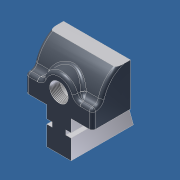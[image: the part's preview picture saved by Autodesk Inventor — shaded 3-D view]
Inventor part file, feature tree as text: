
AUTODESK INVENTOR PART (.ipt)
format: ipt  version: unknown  size: 439,296 bytes
history: native  units: in
note: dims shown in document units (in); Inventor stores cm internally (conversion verified against a paired STEP export)
features: sketch x11, hole x6, extrude x5, fillet x5, projected_geometry x2
ambient origin geometry x8: Origin, YZ Plane, XZ Plane, XY Plane, X Axis, Y Axis, Z Axis, Center Point
bodies: Solid1 (feature_tree)
feature tree (29):
  extrude  "Extrusion1"  Depth=0.875in
  extrude  "Extrusion2"  Depth=0.5055in
  extrude  "Extrusion3"  Depth=1.5in
  extrude  "Extrusion4"  Depth=0.1875in
  extrude  "Extrusion5"  Depth=0.218in
  fillet  "Fillet1"  Radius=0.218in
  hole  "Hole2"  [1 undecoded]
  fillet  "Fillet7"  Radius=0.125in
  fillet  "Fillet8"  Radius=1.187in
  fillet  "Fillet9"  Radius=2.75in
  fillet  "Fillet10"  Radius=0.75in
  hole  "Hole3"  [1 undecoded]
  hole  "Hole4"  [1 undecoded]
  hole  "Hole5"  [1 undecoded]
  hole  "Hole6"  [1 undecoded]
  hole  "Hole7"  [1 undecoded]
  sketch  "Sketch1"  dims[d0=0.997in d1=0.875in]
  sketch  "Sketch2"  dims[d2=0.875in d3=0.5055in]
  sketch  "Sketch3"  dims[d4=0.5055in d5=1.5in]
  sketch  "Sketch6"  dims[d6=1.5in d7=0.1875in]
  sketch  "Sketch7"  dims[d8=0.1875in d9=0.218in d10=0.218in]
  projected_geometry  "Projected Loop1"
  projected_geometry  "Projected Loop2"
  sketch  "Sketch9"  dims[d11=3.25in d12=1.562in d13=0.0in d16=0.125in d17=1.187in d18=2.75in d19=0.75in]
  sketch  "Sketch10"  dims[d20=3.0in d21=0.0in d22=2.187in]
  sketch  "Sketch11"  dims[d23=1.374in d24=1.0in d25=0.0in]
  sketch  "Sketch12"  dims[d26=0.125in d27=1.0in d28=0.0in]
  sketch  "Sketch13"  dims[d29=0.375in d30=1.0in d31=0.0in]
  sketch  "Sketch14"  dims[d32=0.125in d45=1.0in d46=1.0in d47=0.625in d49=1.5in d50=2.75in d51=0.196in d52=0.437in d53=0.375in d54=0.25in d55=0.5635in d56=0.625in d57=0.0in d58=0.25in d59=0.125in d60=0.125in d61=0.125in d65=0.186in d66=0.186in d67=0.625in d68=1.187in d69=0.1495in d70=0.437in d71=0.375in d72=0.25in d73=0.5635in d74=1.062in d75=0.0in d76=0.171in d77=0.437in d78=0.375in d79=0.25in d80=0.5635in d81=0.75in d82=0.0in d83=0.218in d84=0.437in d85=0.375in d86=0.25in d87=0.5635in d88=0.375in d89=0.0in d91=0.749in d92=0.75in d93=0.375in d94=0.25in d95=0.5635in d96=1.187in d97=0.0in d98=0.758in d99=0.75in d100=0.375in d101=0.25in d102=0.5635in d103=0.437in d104=0.0in]
note: 6 required parameter values undecoded (feature->parameter linkage not recoverable at this tier; creation-order binding heuristic only, values carry confidence <= 0.55)
